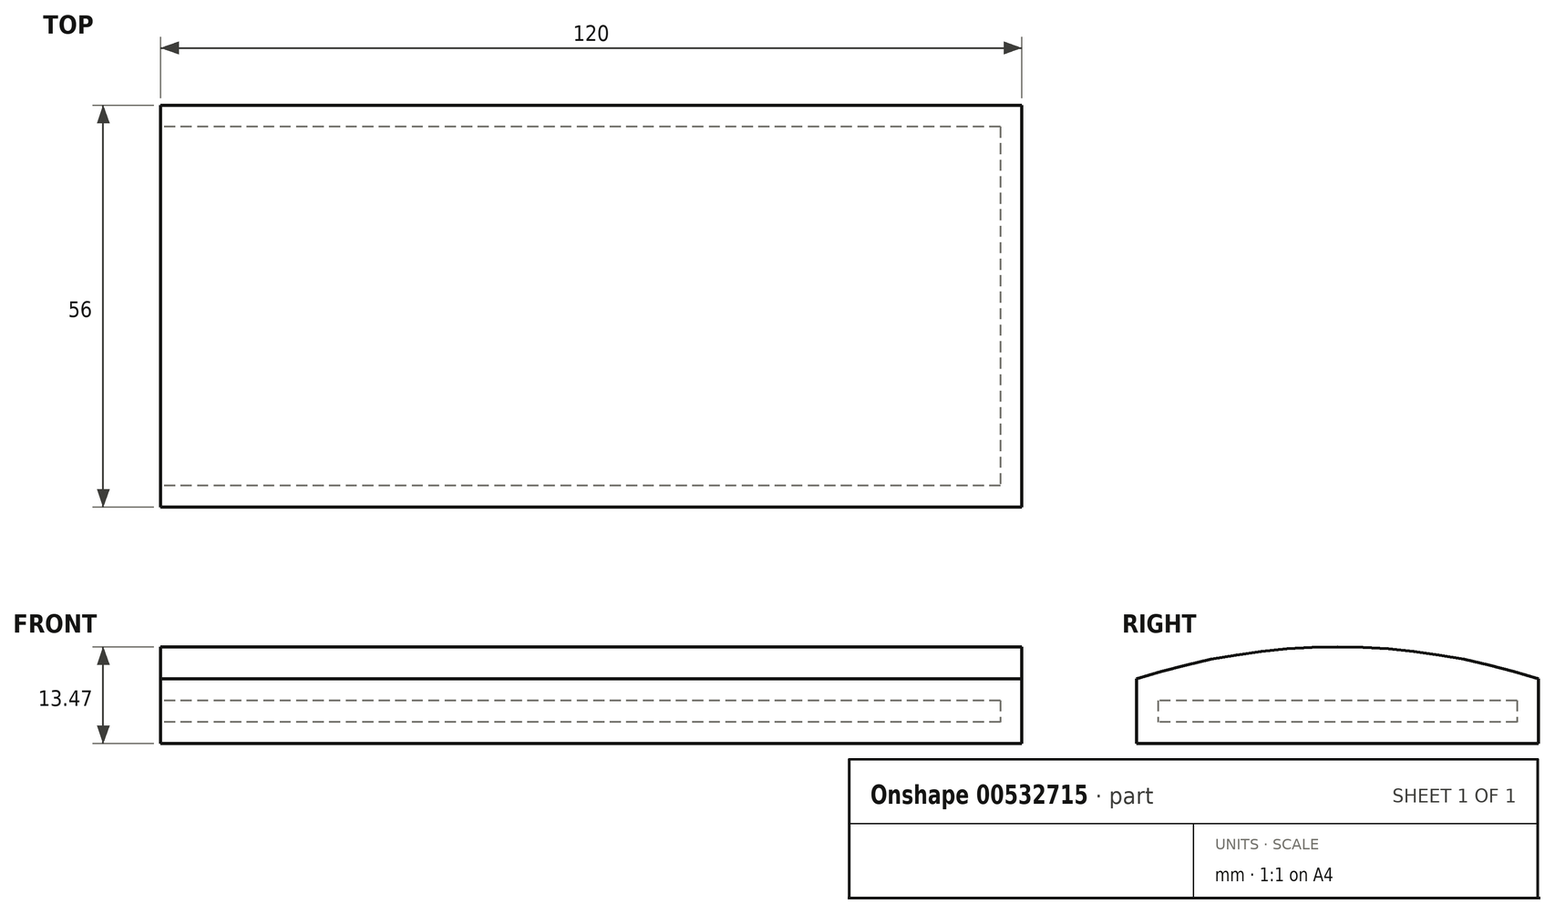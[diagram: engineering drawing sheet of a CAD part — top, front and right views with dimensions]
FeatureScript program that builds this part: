
annotation { "Feature Type Name" : "Feature", "Feature Type Description" : "" }
export const myFeature = defineFeature(function(context is Context, id is Id, definition is map)
    precondition{}
    {
        {
            var Q0;
            Q0=qCreatedBy(makeId("Right.planeOp"),FACE);
            var sketch = newSketch(context, id + "F0", { "sketchPlane" : qUnion([Q0])});
            skLineSegment(sketch, "E0.top", {"start": v(28, -4.5) * mm, "end": v(-28, -4.5) * mm});
            skLineSegment(sketch, "E0.left", {"start": v(28, 4.5) * mm, "end": v(28, -4.5) * mm});
            skLineSegment(sketch, "E0.right", {"start": v(-28, 4.5) * mm, "end": v(-28, -4.5) * mm});
            skArc(sketch, "E1", {"start": v(28, 4.5) * mm, "mid": v(0, 8.97) * mm, "end": v(-28, 4.5) * mm});
            skSolve(sketch);
        }
        {
            var Q0;
            Q0=qSketchRegion(id+"F0",true);
            extrude(context, id + "F1", {"entities" : qUnion([Q0]), "endBound" : BoundingType.SYMMETRIC, "depth" : 120 * mm});
        }
        {
            var Q0;
            Q0=makeQuery(id+"F1.opExtrude","CAP_FACE",FACE,{"disambiguationData":[OSD([sQuery(id+"F0.wireOp",EDGE,"E0.bottom"),sQuery(id+"F0.wireOp",EDGE,"E0.top"),sQuery(id+"F0.wireOp",EDGE,"E0.left"),sQuery(id+"F0.wireOp",EDGE,"E0.right"),sQuery(id+"F0.wireOp",EDGE,"g34ocrht-rPQt-wPrD-86mF-Q5vO9vs38KqS.bottom"),sQuery(id+"F0.wireOp",EDGE,"g34ocrht-rPQt-wPrD-86mF-Q5vO9vs38KqS.top"),sQuery(id+"F0.wireOp",EDGE,"g34ocrht-rPQt-wPrD-86mF-Q5vO9vs38KqS.left"),sQuery(id+"F0.wireOp",EDGE,"g34ocrht-rPQt-wPrD-86mF-Q5vO9vs38KqS.right")])],"isStart":true});
            var sketch = newSketch(context, id + "F2", { "sketchPlane" : qUnion([Q0])});
            skLineSegment(sketch, "E2.bottom", {"start": v(-28, -4.5) * mm, "end": v(28, -4.5) * mm});
            skLineSegment(sketch, "E2.top", {"start": v(-28, -4.5) * mm, "end": v(28, -4.5) * mm});
            skLineSegment(sketch, "E2.left", {"start": v(-28, -4.5) * mm, "end": v(-28, -4.5) * mm});
            skLineSegment(sketch, "E2.right", {"start": v(28, -4.5) * mm, "end": v(28, -4.5) * mm});
            skLineSegment(sketch, "E3.bottom", {"start": v(-25, 1.5) * mm, "end": v(25, 1.5) * mm});
            skLineSegment(sketch, "E3.top", {"start": v(-25, -1.5) * mm, "end": v(25, -1.5) * mm});
            skLineSegment(sketch, "E3.left", {"start": v(-25, 1.5) * mm, "end": v(-25, -1.5) * mm});
            skLineSegment(sketch, "E3.right", {"start": v(25, 1.5) * mm, "end": v(25, -1.5) * mm});
            skPoint(sketch, "E3.middle", {"position": v(0, 0) * mm});
            skSolve(sketch);
        }
        {
            var Q0;
            Q0=qSketchRegion(id+"F2",true);
            extrude(context, id + "F3", {"entities" : qUnion([Q0]), "operationType" : NewBodyOperationType.REMOVE, "oppositeDirection" : true, "depth" : 117 * mm});
        }
    });
